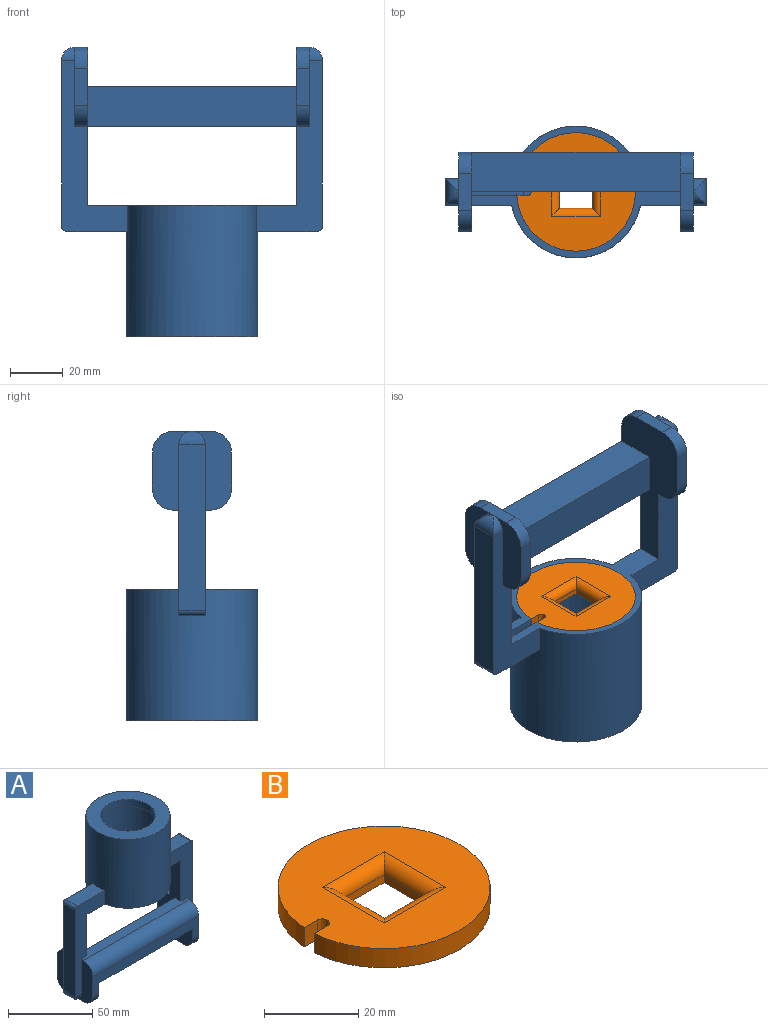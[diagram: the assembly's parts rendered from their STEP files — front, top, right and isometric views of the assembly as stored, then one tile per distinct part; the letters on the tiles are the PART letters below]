
ASSEMBLY  parts=2 mates=1
PART A: 58 faces, bbox 99x50x110 mm
  f0: plane 30x3.5mm, normal (1,0,0), area 104.9mm2, adj f2,f7,f30,f36
  f1: plane 60x30mm, normal (-1,0,0), area 933.8mm2, adj f4,f5,f7,f28,f33,f35,f36,f37
  f2: plane 65x25mm, normal (0,-1,0), area 674.1mm2, adj f0,f7,f12,f15,f16,f26,f36,f42
  f3: plane 65x25mm, normal (0,1,0), area 674.1mm2, adj f6,f7,f12,f15,f16,f26,f40,f41
  f4: plane 65x25mm, normal (0,-1,0), area 674.1mm2, adj f1,f7,f12,f17,f18,f25,f36,f38
  f5: plane 65x25mm, normal (0,1,0), area 674.1mm2, adj f1,f7,f12,f17,f18,f25,f34,f35
  f6: plane 60x30mm, normal (1,0,0), area 738.9mm2, adj f3,f7,f27,f29,f32,f37,f39,f41
  f7: plane 78.99x50mm, normal (0,0,-1), area 615.3mm2, adj f0,f1,f2,f3,f4,f5,f6,f8
  f8: cylinder r=22.5mm len=45mm, axis (0,0,1), area 699.4mm2, adj f7,f9,f22,f23,f24
  f9: plane 45x45mm, normal (0,0,-1), area 333.8mm2, adj f8,f14
  f10: plane 40x40mm, normal (0,0,-1), area 427.1mm2, adj f11,f14
  f11: cylinder r=16.25mm len=32.5mm, axis (0,0,1), area 510.5mm2, adj f10,f13
  f12: cylinder r=25mm len=50mm, axis (0,0,1), area 7652.6mm2, adj f2,f3,f4,f5,f7,f13,f16,f18
  f13: plane 50x50mm, normal (0,0,1), area 1133.9mm2, adj f11,f12
  f14: cylinder r=20mm len=40mm, axis (0,0,1), area 5026.6mm2, adj f9,f10
  f15: plane 63x10mm, normal (-1,0,0), area 630mm2, adj f2,f3,f26,f53
  f16: plane 23x10mm, normal (0,0,1), area 226.6mm2, adj f2,f3,f12,f26
  f17: plane 63x10mm, normal (1,0,0), area 630mm2, adj f4,f5,f25,f56
  f18: plane 23x10mm, normal (0,0,1), area 226.6mm2, adj f4,f5,f12,f25
  f19: plane 2.52x2.52mm, normal (0,-1,0), area 6.2mm2, adj f21,f22,f24,f29
  f20: plane 2.52x2.52mm, normal (0,1,0), area 6.2mm2, adj f21,f22,f23,f30
  f21: plane 3.02x2.51mm, normal (1,0,0), area 7.5mm2, adj f19,f20,f22,f31
  f22: plane 19.54x3.01mm, normal (0,0,-1), area 58.5mm2, adj f8,f19,f20,f21,f23,f24
  f23: plane 17.06x2.52mm, normal (0,1,0), area 42.6mm2, adj f7,f8,f20,f22
  f24: plane 17.06x2.52mm, normal (0,-1,0), area 42.6mm2, adj f7,f8,f19,f22
  f25: cylinder r=2mm len=10mm, axis (0,1,0), area 31.4mm2, adj f4,f5,f17,f18
  f26: cylinder r=2mm len=10mm, axis (0,-1,0), area 31.4mm2, adj f2,f3,f15,f16
  f27: plane 14x5mm, normal (0,0,-1), area 70mm2, adj f6,f40,f42,f45,f47
  f28: plane 14x5mm, normal (0,0,-1), area 70mm2, adj f1,f34,f38,f49,f50
  f29: plane 30.01x2.51mm, normal (0,-1,0), area 70.1mm2, adj f6,f19,f31,f32
  f30: plane 30.01x2.51mm, normal (0,1,0), area 70.1mm2, adj f0,f20,f31,f32
  f31: plane 27.51x3.01mm, normal (1,0,0), area 82.5mm2, adj f21,f29,f30,f32
  f32: cylinder r=2.5mm len=3mm, axis (0,-1,0), area 11.8mm2, adj f6,f29,f30,f31,f36
  f33: plane 14x5mm, normal (0,1,0), area 70mm2, adj f1,f34,f48,f49
  f34: plane 30x15mm, normal (1,0,0), area 277.9mm2, adj f5,f28,f33,f35,f48,f49,f55
  f35: plane 5x2mm, normal (0,0,1), area 10mm2, adj f1,f5,f34,f48
  f36: plane 88.99x7mm, normal (0,0,1), area 572.9mm2, adj f0,f1,f2,f4,f32,f38,f42,f44
  f37: plane 88.99x14mm, normal (0,-1,0), area 692.9mm2, adj f1,f6,f38,f42,f43,f47,f50,f51
  f38: plane 30x15mm, normal (1,0,0), area 277.9mm2, adj f4,f28,f36,f37,f50,f51,f57
  f39: plane 14x5mm, normal (0,1,0), area 70mm2, adj f6,f40,f45,f46
  f40: plane 30x15mm, normal (-1,0,0), area 277.9mm2, adj f3,f27,f39,f41,f45,f46,f54
  f41: plane 5x2mm, normal (0,0,1), area 10mm2, adj f3,f6,f40,f46
  f42: plane 30x15mm, normal (-1,0,0), area 277.9mm2, adj f2,f27,f36,f37,f47,f51,f52
  f43: plane 78.99x15mm, normal (0,0,-1), area 1184.8mm2, adj f1,f6,f37,f44
  f44: plane 78.99x15mm, normal (0,1,0), area 1184.8mm2, adj f1,f6,f36,f43
  f45: cylinder r=8mm len=8mm, axis (1,0,0), area 62.8mm2, adj f6,f27,f39,f40
  f46: cylinder r=8mm len=8mm, axis (-1,0,0), area 62.8mm2, adj f6,f39,f40,f41
  f47: cylinder r=8mm len=8mm, axis (1,0,0), area 62.8mm2, adj f6,f27,f37,f42
  f48: cylinder r=8mm len=8mm, axis (-1,0,0), area 62.8mm2, adj f1,f33,f34,f35
  f49: cylinder r=8mm len=8mm, axis (1,0,0), area 62.8mm2, adj f1,f28,f33,f34
  f50: cylinder r=8mm len=8mm, axis (-1,0,0), area 62.8mm2, adj f1,f28,f37,f38
  f51: cylinder r=8mm len=88.99mm, axis (1,0,0), area 1118.3mm2, adj f36,f37,f38,f42
  f52: cylinder r=5mm len=5mm, axis (-1,0,0), area 19.6mm2, adj f2,f42,f53
  f53: cylinder r=5mm len=10mm, axis (0,1,0), area 39.3mm2, adj f15,f52,f54
  f54: cylinder r=5mm len=5mm, axis (1,0,0), area 19.6mm2, adj f3,f40,f53
  f55: cylinder r=5mm len=5mm, axis (1,0,0), area 19.6mm2, adj f5,f34,f56
  f56: cylinder r=5mm len=10mm, axis (0,-1,0), area 39.3mm2, adj f17,f55,f57
  f57: cylinder r=5mm len=5mm, axis (-1,0,0), area 19.6mm2, adj f4,f38,f56
PART B: 14 faces, bbox 45x45x5 mm
  f0: cylinder r=1.5mm len=5mm, axis (0,0,-1), area 22.6mm2, adj f1,f7,f8,f9
  f1: plane 5x4mm, normal (0,1,0), area 20mm2, adj f0,f2,f8,f9
  f2: cylinder r=22.5mm len=45mm, axis (0,0,-1), area 691.8mm2, adj f1,f7,f8,f9
  f3: plane 12.5x2mm, normal (-1,0,0), area 25mm2, adj f4,f6,f9,f11
  f4: plane 12.5x2mm, normal (0,1,0), area 25mm2, adj f3,f5,f9,f10
  f5: plane 12.5x2mm, normal (1,0,0), area 25mm2, adj f4,f6,f9,f12
  f6: plane 12.5x2mm, normal (0,-1,0), area 25mm2, adj f3,f5,f9,f13
  f7: plane 5x4mm, normal (0,-1,0), area 20mm2, adj f0,f2,f8,f9
  f8: plane 45x44.95mm, normal (0,0,1), area 1232.8mm2, adj f0,f1,f2,f7,f10,f11,f12,f13
  f9: plane 45x44.95mm, normal (0,0,-1), area 1418.8mm2, adj f0,f1,f2,f3,f4,f5,f6,f7
  f10: cylinder r=3mm len=18.5mm, axis (1,0,0), area 69.2mm2, adj f4,f8,f11,f12
  f11: cylinder r=3mm len=18.5mm, axis (0,1,0), area 69.2mm2, adj f3,f8,f10,f13
  f12: cylinder r=3mm len=18.5mm, axis (0,-1,0), area 69.2mm2, adj f5,f8,f10,f13
  f13: cylinder r=3mm len=18.5mm, axis (-1,0,0), area 69.2mm2, adj f6,f8,f11,f12
PLACE A rot(axis=(1,0,0),180deg) t=(-103.98,14.21,-97.32)mm
PLACE B t=(-103.98,14.21,-52.32)mm
MATE fastened A.f14 <-> B.f2  axis (0,0,-1) through (-103.98,14.21,-52.32)mm
